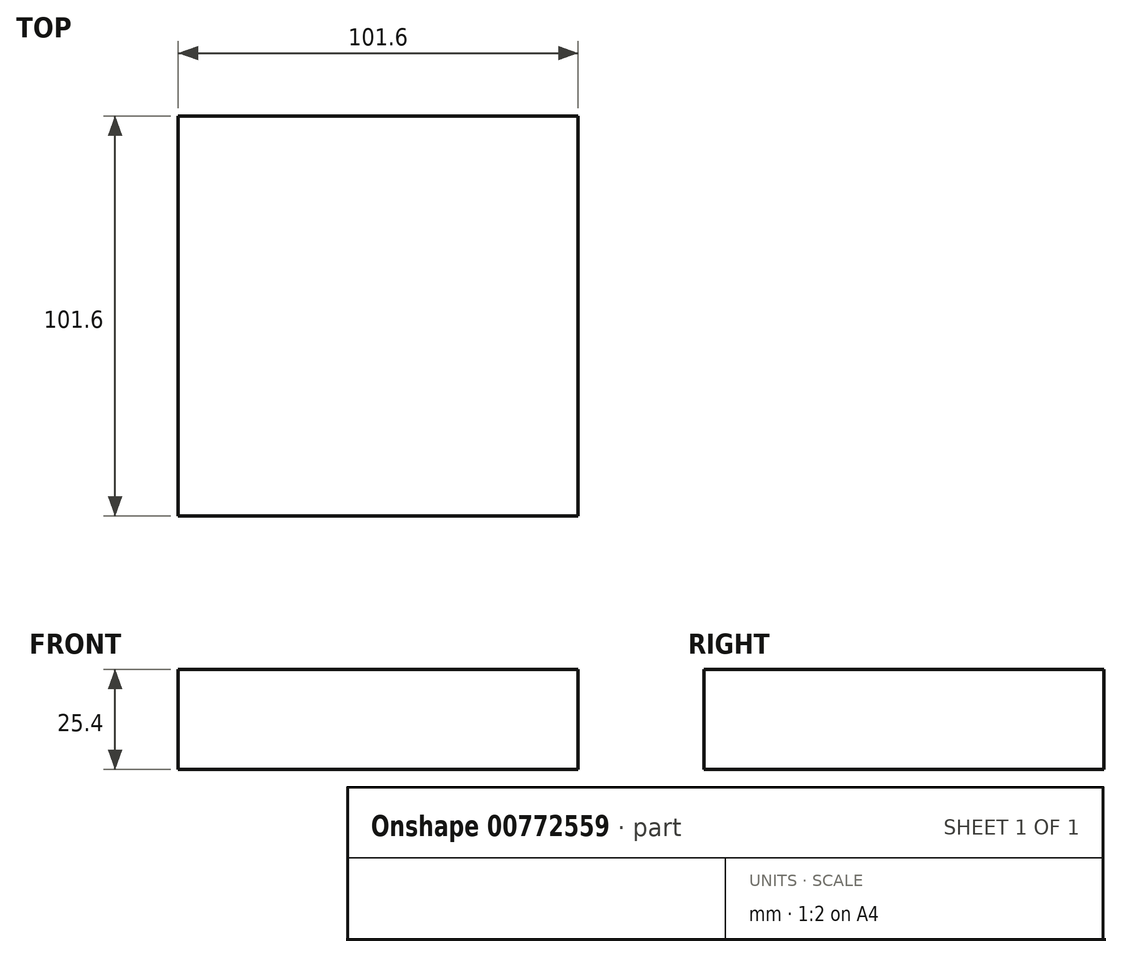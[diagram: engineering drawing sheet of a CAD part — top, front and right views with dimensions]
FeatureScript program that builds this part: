
annotation { "Feature Type Name" : "Feature", "Feature Type Description" : "" }
export const myFeature = defineFeature(function(context is Context, id is Id, definition is map)
    precondition{}
    {
        {
            var Q0;
            Q0=qCreatedBy(makeId("Top.planeOp"),FACE);
            var sketch = newSketch(context, id + "F0", { "sketchPlane" : qUnion([Q0])});
            skLineSegment(sketch, "E0.bottom", {"start": v(-50.8, 50.8) * mm, "end": v(50.8, 50.8) * mm});
            skLineSegment(sketch, "E0.top", {"start": v(-50.8, -50.8) * mm, "end": v(50.8, -50.8) * mm});
            skLineSegment(sketch, "E0.left", {"start": v(-50.8, 50.8) * mm, "end": v(-50.8, -50.8) * mm});
            skLineSegment(sketch, "E0.right", {"start": v(50.8, 50.8) * mm, "end": v(50.8, -50.8) * mm});
            skPoint(sketch, "E0.middle", {"position": v(0, 0) * mm});
            skSolve(sketch);
        }
        {
            var Q0;
            Q0=makeQuery(id+"F0.imprint","IMPRINT",FACE,{"disambiguationData":[TD([[makeQuery(id+"F0.imprint","IMPRINT",EDGE,{"derivedFrom":sQuery(id+"F0.wireOp",EDGE,"E0.bottom")}),-1.0]])]});
            extrude(context, id + "F1", {"entities" : qUnion([Q0]), "depth" : 25.4 * mm, "offsetDistance" : 25.4 * mm});
        }
    });
